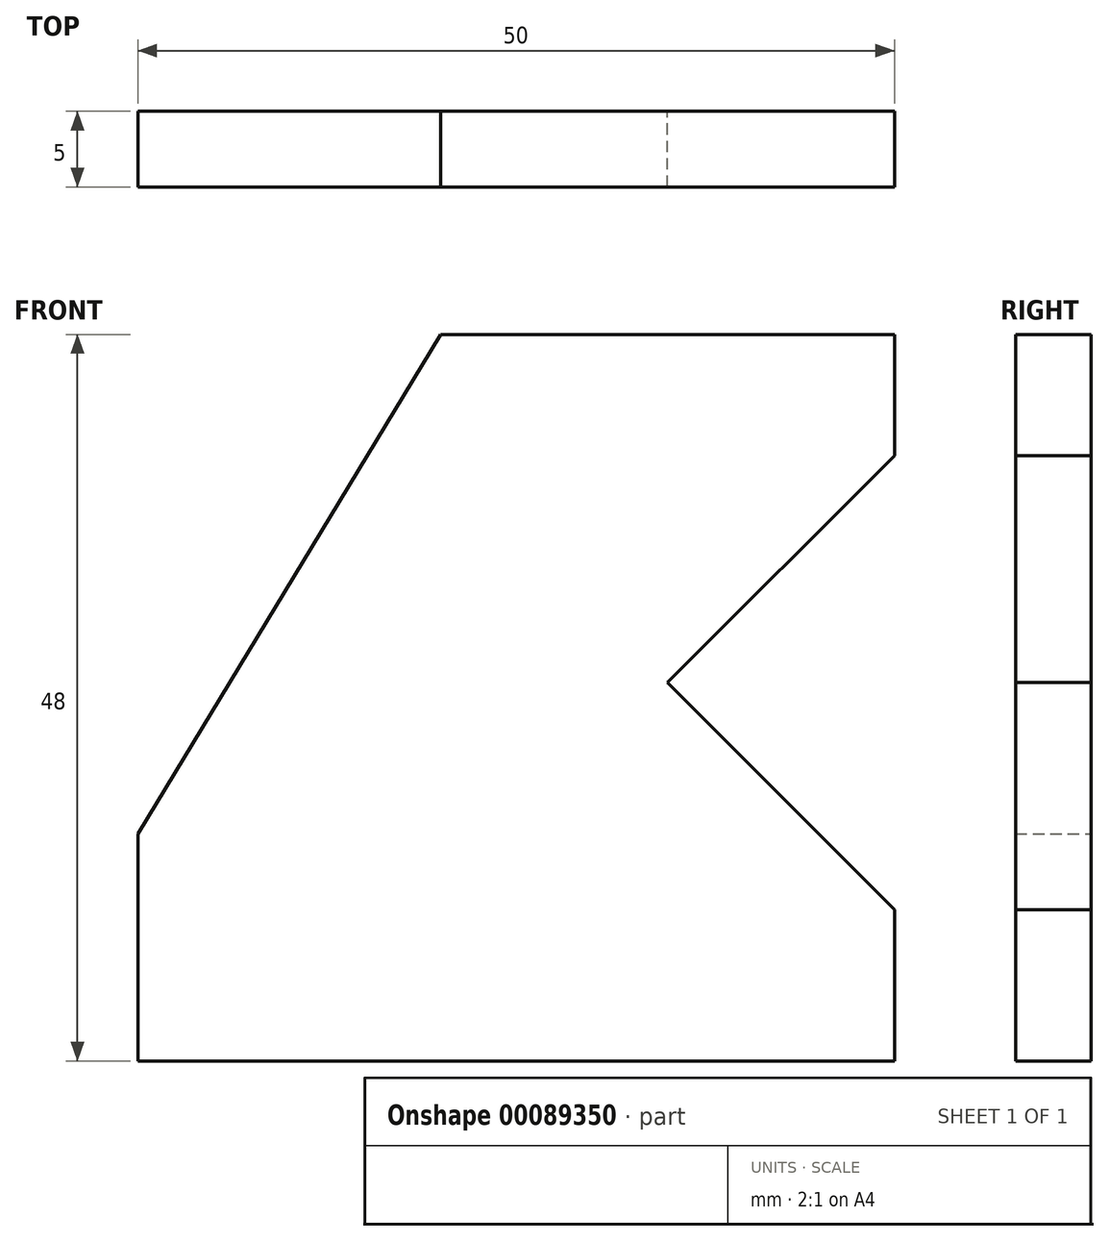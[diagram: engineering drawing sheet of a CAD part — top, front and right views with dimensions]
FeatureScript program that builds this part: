
annotation { "Feature Type Name" : "Feature", "Feature Type Description" : "" }
export const myFeature = defineFeature(function(context is Context, id is Id, definition is map)
    precondition{}
    {
        {
            var Q0;
            Q0=qCreatedBy(makeId("Front.planeOp"),FACE);
            var sketch = newSketch(context, id + "F0", { "sketchPlane" : qUnion([Q0])});
            skLineSegment(sketch, "E0", {"start": v(0, 0) * mm, "end": v(0, 15) * mm});
            skLineSegment(sketch, "E1", {"start": v(0, 15) * mm, "end": v(20, 48) * mm});
            skLineSegment(sketch, "E2", {"start": v(20, 48) * mm, "end": v(50, 48) * mm});
            skLineSegment(sketch, "E3", {"start": v(50, 48) * mm, "end": v(50, 40) * mm});
            skLineSegment(sketch, "E4", {"start": v(50, 40) * mm, "end": v(35, 25) * mm});
            skLineSegment(sketch, "E5", {"start": v(35, 25) * mm, "end": v(50, 10) * mm});
            skLineSegment(sketch, "E6", {"start": v(50, 10) * mm, "end": v(50, 0) * mm});
            skLineSegment(sketch, "E7", {"start": v(50, 0) * mm, "end": v(0, 0) * mm});
            skLineSegment(sketch, "E8", {"start": v(25.68, 25) * mm, "end": v(50.47, 25) * mm, "construction": true});
            skSolve(sketch);
        }
        {
            var Q0;
            Q0 = qSketchRegion(id + "F0", true);
            extrude(context, id + "F1", {"entities" : qUnion([Q0]), "depth" : 5 * mm});
        }
    });
